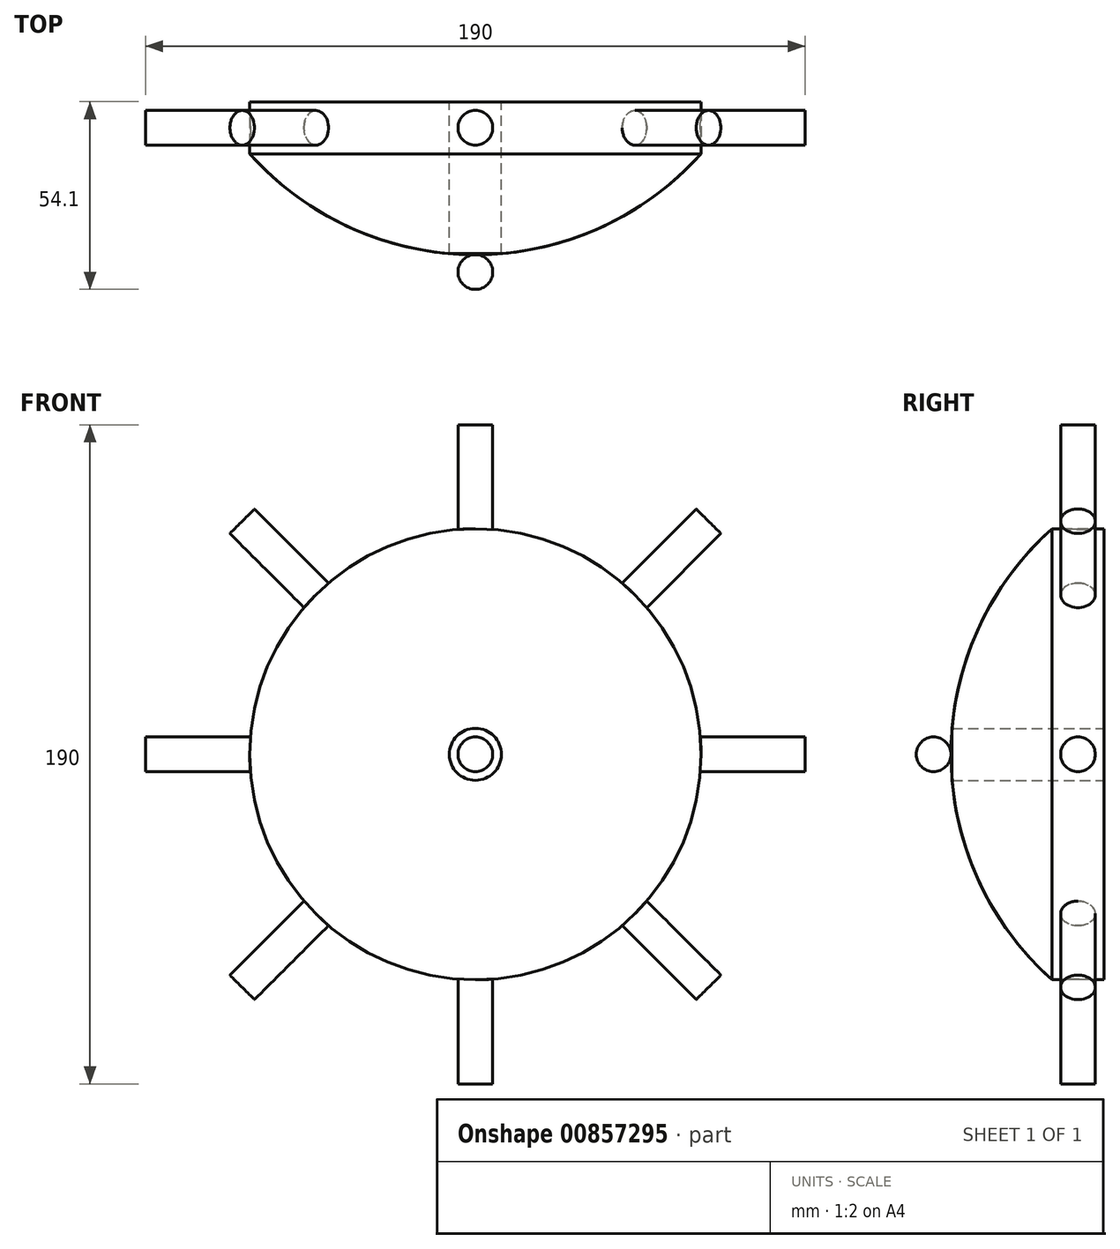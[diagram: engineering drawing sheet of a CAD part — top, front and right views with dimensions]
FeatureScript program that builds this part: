
annotation { "Feature Type Name" : "Feature", "Feature Type Description" : "" }
export const myFeature = defineFeature(function(context is Context, id is Id, definition is map)
    precondition{}
    {
        {
            var Q0;
            Q0=qCreatedBy(makeId("Right.planeOp"),FACE);
            var sketch = newSketch(context, id + "F0", { "sketchPlane" : qUnion([Q0])});
            skLineSegment(sketch, "E0", {"start": v(-120.38, 0) * mm, "end": v(1.6, 0) * mm, "construction": true});
            skLineSegment(sketch, "E1", {"start": v(-97.2, 0) * mm, "end": v(-97.2, 65) * mm});
            skLineSegment(sketch, "E2", {"start": v(-97.2, 65) * mm, "end": v(-112.2, 65) * mm});
            skLineSegment(sketch, "E3", {"start": v(-112.2, 65) * mm, "end": v(-112.2, 0) * mm});
            skLineSegment(sketch, "E4", {"start": v(-97.2, 0) * mm, "end": v(-112.2, 0) * mm});
            skSolve(sketch);
        }
        {
            var Q0;
            Q0 = qSketchRegion(id + "F0", true);
            var Q1;
            Q1=sQuery(id+"F0.wireOp",EDGE,"E0");
            revolve(context, id + "F1", {"surfaceOperationType" : NewSurfaceOperationType.NEW, "entities" : qUnion([Q0]), "axis" : qUnion([Q1]), "revolveType" : RevolveType.FULL});
        }
        {
            var Q0;
            Q0=qCreatedBy(makeId("Right.planeOp"),FACE);
            var sketch = newSketch(context, id + "F2", { "sketchPlane" : qUnion([Q0])});
            skLineSegment(sketch, "E5.0", {"start": v(-112.2, -65) * mm, "end": v(-112.2, 65) * mm, "construction": true});
            skLineSegment(sketch, "E6", {"start": v(-112.2, -65) * mm, "end": v(-112.2, 0) * mm});
            skLineSegment(sketch, "E7", {"start": v(-112.2, 0) * mm, "end": v(-141.3, 0) * mm});
            skArc(sketch, "E8", {"start": v(-141.3, 0) * mm, "mid": v(-133.7, -35.6) * mm, "end": v(-112.2, -65) * mm});
            skSolve(sketch);
        }
        {
            var Q0;
            Q0=makeQuery(id+"F2.imprint","IMPRINT",FACE,{"disambiguationData":[TD([[makeQuery(id+"F2.imprint","IMPRINT",EDGE,{"derivedFrom":sQuery(id+"F2.wireOp",EDGE,"E6")}),1.0]])]});
            var Q1;
            Q1=sQuery(id+"F0.wireOp",EDGE,"E0");
            revolve(context, id + "F3", {"operationType" : NewBodyOperationType.ADD, "surfaceOperationType" : NewSurfaceOperationType.NEW, "entities" : qUnion([Q0]), "axis" : qUnion([Q1]), "revolveType" : RevolveType.FULL});
        }
        {
            var Q0;
            Q0=qCreatedBy(makeId("Right.planeOp"),FACE);
            var sketch = newSketch(context, id + "F4", { "sketchPlane" : qUnion([Q0])});
            skArc(sketch, "E9", {"start": v(-112.2, 65) * mm, "mid": v(-141.3, 0) * mm, "end": v(-112.2, -65) * mm, "construction": true});
            skLineSegment(sketch, "E10", {"start": v(-141.3, 0) * mm, "end": v(-151.3, 0) * mm});
            skPoint(sketch, "E10.endSnap0", {"position": v(-141.3, 0) * mm});
            skArc(sketch, "E11", {"start": v(-141.3, 0) * mm, "mid": v(-146.3, 5) * mm, "end": v(-151.3, 0) * mm});
            skSolve(sketch);
        }
        {
            var Q0;
            Q0 = qSketchRegion(id + "F4", true);
            var Q1;
            Q1=sQuery(id+"F0.wireOp",EDGE,"E0");
            revolve(context, id + "F5", {"operationType" : NewBodyOperationType.ADD, "surfaceOperationType" : NewSurfaceOperationType.NEW, "entities" : qUnion([Q0]), "axis" : qUnion([Q1]), "revolveType" : RevolveType.FULL});
        }
        {
            var Q0;
            Q0=qCreatedBy(makeId("Right.planeOp"),FACE);
            var sketch = newSketch(context, id + "F6", { "sketchPlane" : qUnion([Q0])});
            skLineSegment(sketch, "E12", {"start": v(-112.2, 65) * mm, "end": v(-97.2, 65) * mm, "construction": true});
            skLineSegment(sketch, "E13.bottom", {"start": v(-104.7, 65) * mm, "end": v(-99.7, 65) * mm});
            skLineSegment(sketch, "E13.top", {"start": v(-104.7, 95) * mm, "end": v(-99.7, 95) * mm});
            skLineSegment(sketch, "E13.left", {"start": v(-104.7, 65) * mm, "end": v(-104.7, 95) * mm});
            skLineSegment(sketch, "E13.right", {"start": v(-99.7, 65) * mm, "end": v(-99.7, 95) * mm});
            skLineSegment(sketch, "E14", {"start": v(-104.7, 65) * mm, "end": v(-104.7, 110.47) * mm, "construction": true});
            skLineSegment(sketch, "E15.top", {"start": v(-104.7, 63.23) * mm, "end": v(-99.7, 63.23) * mm});
            skLineSegment(sketch, "E15.left", {"start": v(-104.7, 65) * mm, "end": v(-104.7, 63.23) * mm});
            skLineSegment(sketch, "E15.right", {"start": v(-99.7, 65) * mm, "end": v(-99.7, 63.23) * mm});
            skSolve(sketch);
        }
        {
            var Q0;
            Q0 = qSketchRegion(id + "F6", true);
            var Q1;
            Q1=sQuery(id+"F6.wireOp",EDGE,"E14");
            revolve(context, id + "F7", {"operationType" : NewBodyOperationType.ADD, "surfaceOperationType" : NewSurfaceOperationType.NEW, "entities" : qUnion([Q0]), "axis" : qUnion([Q1]), "revolveType" : RevolveType.FULL});
        }
        {
            var Q0;
            Q0=makeQuery(id+"F1.opRevolve","SWEPT_BODY",BODY,{"disambiguationData":[OSD([sQuery(id+"F0.wireOp",EDGE,"E1"),sQuery(id+"F0.wireOp",EDGE,"E2"),sQuery(id+"F0.wireOp",EDGE,"E3"),sQuery(id+"F0.wireOp",EDGE,"E4")])]});
            var Q1;
            Q1=sQuery(id+"F0.wireOp",EDGE,"E0");
            circularPattern(context, id + "F8", {"operationType" : NewBodyOperationType.ADD, "entities" : qUnion([Q0]), "axis" : qUnion([Q1]), "angle" : 360 * degree, "instanceCount" : 8, "equalSpace" : true});
        }
        {
            var Q0;
            Q0=makeQuery(id+"F1.opRevolve","SWEPT_FACE",FACE,{"disambiguationData":[OSD([sQuery(id+"F0.wireOp",EDGE,"E1")])]});
            var sketch = newSketch(context, id + "F9", { "sketchPlane" : qUnion([Q0])});
            skPoint(sketch, "E16", {"position": v(0, 0) * mm});
            skSolve(sketch);
        }
        {
            var Q0;
            Q0=sQuery(id+"F9.wireOp",VERTEX,"E16");
            var Q1;
            Q1=makeQuery(id+"F1.opRevolve","SWEPT_BODY",BODY,{"disambiguationData":[OSD([sQuery(id+"F0.wireOp",EDGE,"E1"),sQuery(id+"F0.wireOp",EDGE,"E2"),sQuery(id+"F0.wireOp",EDGE,"E3"),sQuery(id+"F0.wireOp",EDGE,"E4")])]});
            hole(context, id + "F10", {"style" : HoleStyle.SIMPLE, "endStyle" : HoleEndStyle.THROUGH, "holeDiameter" : 15 * mm, "majorDiameter" : 5 * mm, "isTappedThrough" : true, "tappedDepth" : 12 * mm, "tapClearance" : 3, "locations" : qUnion([Q0]), "scope" : qUnion([Q1])});
        }
    });
